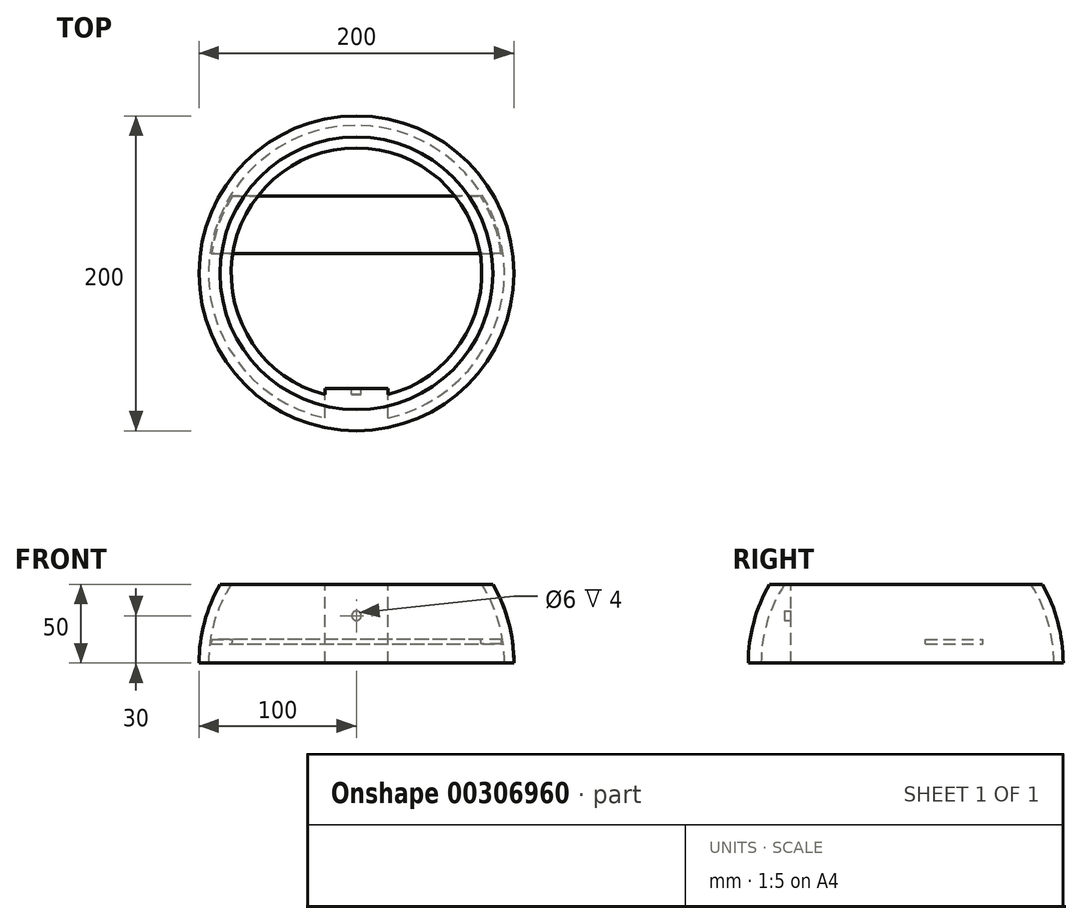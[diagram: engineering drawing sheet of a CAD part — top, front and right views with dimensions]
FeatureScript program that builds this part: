
annotation { "Feature Type Name" : "Feature", "Feature Type Description" : "" }
export const myFeature = defineFeature(function(context is Context, id is Id, definition is map)
    precondition{}
    {
        {
            var Q0;
            Q0=qCreatedBy(makeId("Front.planeOp"),FACE);
            var sketch = newSketch(context, id + "F0", { "sketchPlane" : qUnion([Q0])});
            skArc(sketch, "E0", {"start": v(-86.6, 50) * mm, "mid": v(-96.6, 25.88) * mm, "end": v(-100, 0) * mm});
            skLineSegment(sketch, "E1", {"start": v(0, 50) * mm, "end": v(0, 0) * mm});
            skLineSegment(sketch, "E2", {"start": v(0, 50) * mm, "end": v(-86.6, 50) * mm});
            skLineSegment(sketch, "E3", {"start": v(0, 0) * mm, "end": v(-100, 0) * mm});
            skPoint(sketch, "E4.orphan", {"position": v(0, 100) * mm});
            skSolve(sketch);
        }
        {
            var Q0;
            Q0 = qSketchRegion(id + "F0", true);
            var Q1;
            Q1=sQuery(id+"F0.wireOp",EDGE,"E1");
            revolve(context, id + "F1", {"entities" : qUnion([Q0]), "axis" : qUnion([Q1]), "revolveType" : RevolveType.FULL});
        }
        {
            var Q0;
            Q0=makeQuery(id+"F1.opRevolve","SWEPT_FACE",FACE,{"disambiguationData":[OSD([sQuery(id+"F0.wireOp",EDGE,"E2")])]});
            var Q1;
            Q1=makeQuery(id+"F1.opRevolve","SWEPT_FACE",FACE,{"disambiguationData":[OSD([sQuery(id+"F0.wireOp",EDGE,"E3")])]});
            shell(context, id + "F2", {"entities" : qUnion([Q0, Q1]), "thickness" : 6 * mm});
        }
        {
            var Q0;
            Q0=qCreatedBy(makeId("Front.planeOp"),FACE);
            cPlane(context, id + "F3", {"entities" : qUnion([Q0]), "cplaneType" : CPlaneType.OFFSET, "offset" : 49 * mm, "oppositeDirection" : true, "width" : 150 * mm, "height" : 150 * mm});
        }
        {
            var Q0;
            Q0=qCreatedBy(id+"F3.planeOp",FACE);
            var sketch = newSketch(context, id + "F4", { "sketchPlane" : qUnion([Q0])});
            skLineSegment(sketch, "E5", {"start": v(47.2, 15) * mm, "end": v(-12.8, 15) * mm});
            skLineSegment(sketch, "E6", {"start": v(-12.8, 15) * mm, "end": v(-12.8, 12) * mm});
            skLineSegment(sketch, "E7", {"start": v(-12.8, 12) * mm, "end": v(47.2, 12) * mm});
            skLineSegment(sketch, "E8", {"start": v(47.2, 12) * mm, "end": v(47.2, 15) * mm});
            skSolve(sketch);
        }
        {
            var Q0;
            Q0 = qSketchRegion(id + "F4", true);
            extrude(context, id + "F5", {"entities" : qUnion([Q0]), "depth" : 36.5 * mm});
        }
        {
            var Q0;
            Q0=makeQuery(id+"F5.opExtrude","SWEPT_FACE",FACE,{"disambiguationData":[OSD([sQuery(id+"F4.wireOp",EDGE,"E8")])]});
            extrude(context, id + "F6", {"entities" : qUnion([Q0]), "operationType" : NewBodyOperationType.ADD, "endBound" : BoundingType.UP_TO_NEXT, "depth" : 25 * mm});
        }
        {
            var Q0;
            Q0=makeQuery(id+"F5.opExtrude","SWEPT_FACE",FACE,{"disambiguationData":[OSD([sQuery(id+"F4.wireOp",EDGE,"E6")])]});
            extrude(context, id + "F7", {"entities" : qUnion([Q0]), "operationType" : NewBodyOperationType.ADD, "endBound" : BoundingType.UP_TO_NEXT, "depth" : 25 * mm});
        }
        {
            var Q0;
            Q0=qCreatedBy(makeId("Front.planeOp"),FACE);
            cPlane(context, id + "F8", {"entities" : qUnion([Q0]), "cplaneType" : CPlaneType.OFFSET, "offset" : 62 * mm, "width" : 150 * mm, "height" : 150 * mm});
        }
        {
            var Q0;
            Q0=qCreatedBy(id+"F8.planeOp",FACE);
            var sketch = newSketch(context, id + "F9", { "sketchPlane" : qUnion([Q0])});
            skLineSegment(sketch, "E9", {"start": v(20, 0) * mm, "end": v(20, 50) * mm});
            skLineSegment(sketch, "E10", {"start": v(-20, 0) * mm, "end": v(-20, 50) * mm});
            skLineSegment(sketch, "E11.0", {"start": v(-20, 0) * mm, "end": v(20, 0) * mm});
            skLineSegment(sketch, "E12.0", {"start": v(-20, 50) * mm, "end": v(20, 50) * mm});
            skPoint(sketch, "E13.orphan", {"position": v(-100, 0) * mm});
            skPoint(sketch, "E14.orphan", {"position": v(-86.6, 50) * mm});
            skPoint(sketch, "E15.orphan", {"position": v(100, 0) * mm});
            skPoint(sketch, "E16.orphan", {"position": v(86.6, 50) * mm});
            skSolve(sketch);
        }
        {
            var Q0;
            Q0 = qSketchRegion(id + "F9", true);
            extrude(context, id + "F10", {"entities" : qUnion([Q0]), "operationType" : NewBodyOperationType.ADD, "endBound" : BoundingType.UP_TO_NEXT, "depth" : 25 * mm});
        }
        {
            var Q0;
            Q0=makeQuery(id+"F10.opExtrude","CAP_FACE",FACE,{"disambiguationData":[OSD([sQuery(id+"F9.wireOp",EDGE,"E9"),sQuery(id+"F9.wireOp",EDGE,"E10"),sQuery(id+"F9.wireOp",EDGE,"E11.0"),sQuery(id+"F9.wireOp",EDGE,"E12.0")])],"isStart":true});
            var sketch = newSketch(context, id + "F11", { "sketchPlane" : qUnion([Q0])});
            skCircle(sketch, "E17", {"center": v(0, 30) * mm, "radius": 3 * mm});
            skSolve(sketch);
        }
        {
            var Q0;
            Q0=makeQuery(id+"F11.imprint","IMPRINT",FACE,{"disambiguationData":[TD([[makeQuery(id+"F11.imprint","IMPRINT",EDGE,{"derivedFrom":sQuery(id+"F11.wireOp",EDGE,"E17")}),1.0]])]});
            extrude(context, id + "F12", {"entities" : qUnion([Q0]), "operationType" : NewBodyOperationType.REMOVE, "oppositeDirection" : true, "depth" : 4 * mm});
        }
        {
            var Q0;
            Q0=makeQuery(id+"F10.opExtrude","CAP_FACE",FACE,{"disambiguationData":[OSD([sQuery(id+"F9.wireOp",EDGE,"E9"),sQuery(id+"F9.wireOp",EDGE,"E10"),sQuery(id+"F9.wireOp",EDGE,"E11.0"),sQuery(id+"F9.wireOp",EDGE,"E12.0")])],"isStart":true});
            extrude(context, id + "F13", {"entities" : qUnion([Q0]), "operationType" : NewBodyOperationType.REMOVE, "oppositeDirection" : true, "depth" : 11 * mm});
        }
        {
            var Q0;
            Q0=makeQuery(id+"F12.boolean.opBoolean","COPY",FACE,{"derivedFrom":makeQuery(id+"F12.opExtrude","CAP_FACE",FACE,{"disambiguationData":[OSD([sQuery(id+"F11.wireOp",EDGE,"E17")])],"isStart":false})});
            extrude(context, id + "F14", {"entities" : qUnion([Q0]), "operationType" : NewBodyOperationType.REMOVE, "oppositeDirection" : true, "depth" : 11 * mm});
        }
    });
